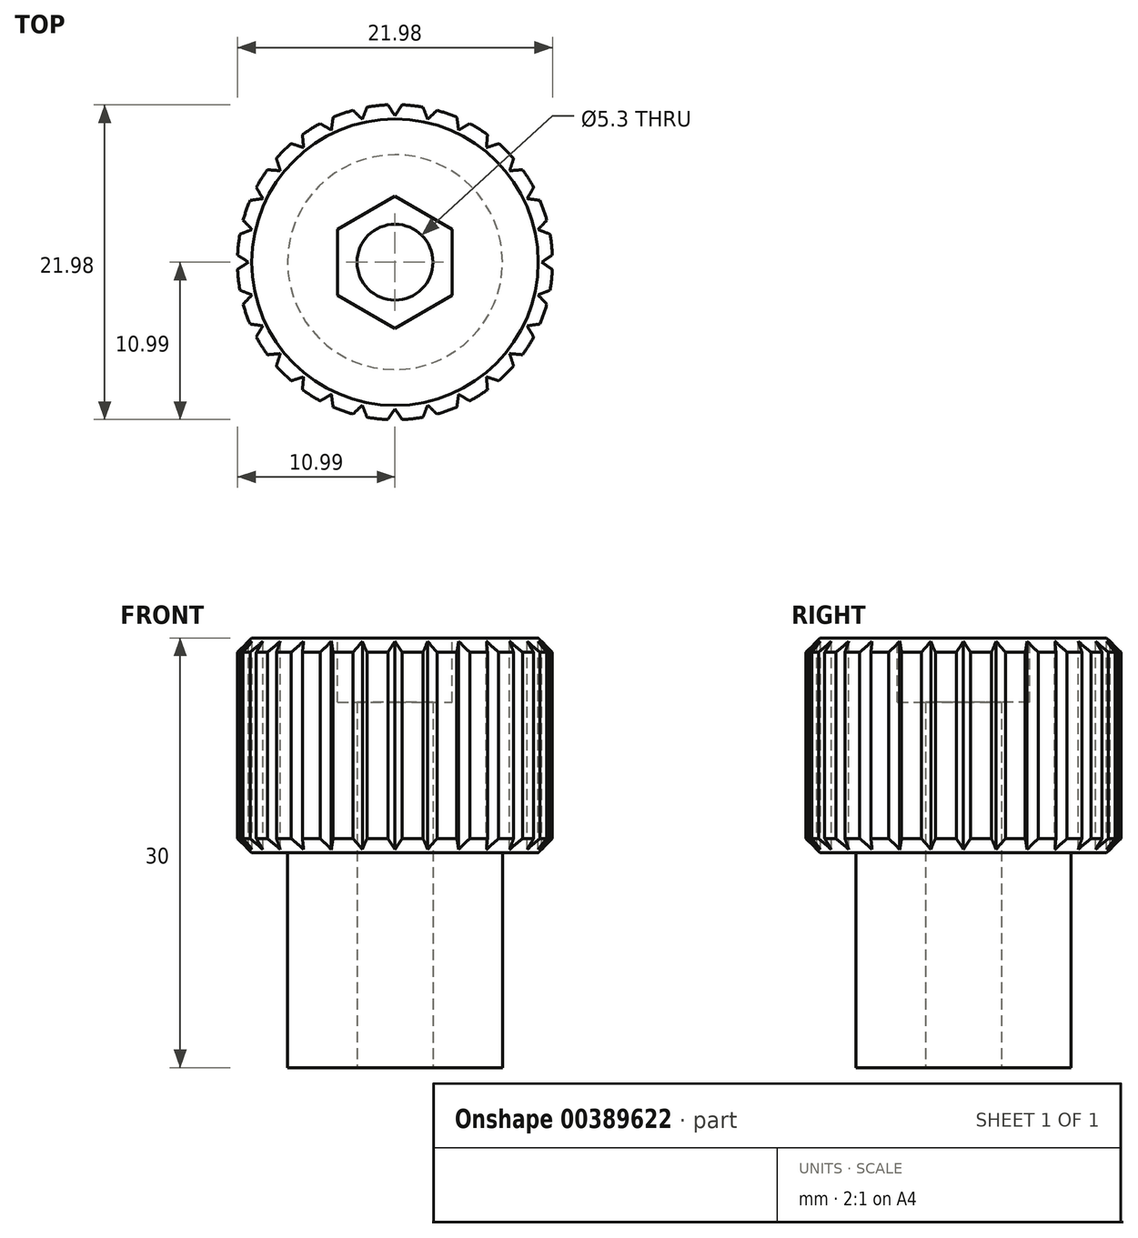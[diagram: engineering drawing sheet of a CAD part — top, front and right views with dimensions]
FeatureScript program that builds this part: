
annotation { "Feature Type Name" : "Feature", "Feature Type Description" : "" }
export const myFeature = defineFeature(function(context is Context, id is Id, definition is map)
    precondition{}
    {
        {
            var Q0;
            Q0=qCreatedBy(makeId("Top.planeOp"),FACE);
            var sketch = newSketch(context, id + "F0", { "sketchPlane" : qUnion([Q0])});
            skCircle(sketch, "E0", {"center": v(0, 0) * mm, "radius": 2.65 * mm});
            skCircle(sketch, "E1", {"center": v(0, 0) * mm, "radius": 7.5 * mm});
            skSolve(sketch);
        }
        {
            var Q0;
            Q0 = qSketchRegion(id + "F0", true);
            extrude(context, id + "F1", {"entities" : qUnion([Q0]), "depth" : 15 * mm});
        }
        {
            var Q0;
            Q0=makeQuery(id+"F1.opExtrude","CAP_FACE",FACE,{"disambiguationData":[OSD([sQuery(id+"F0.wireOp",EDGE,"E0"),sQuery(id+"F0.wireOp",EDGE,"E1")])],"isStart":false});
            var sketch = newSketch(context, id + "F2", { "sketchPlane" : qUnion([Q0])});
            skCircle(sketch, "E2", {"center": v(0, 0) * mm, "radius": 11 * mm});
            skSolve(sketch);
        }
        {
            var Q0;
            Q0 = qSketchRegion(id + "F2", true);
            extrude(context, id + "F3", {"entities" : qUnion([Q0]), "operationType" : NewBodyOperationType.ADD, "depth" : 15 * mm});
        }
        {
            var Q0;
            Q0 = qSketchRegion(id + "F2", true);
            extrude(context, id + "F4", {"entities" : qUnion([Q0]), "operationType" : NewBodyOperationType.ADD, "depth" : 15 * mm});
        }
        {
            var Q0;
            Q0=makeQuery(id+"F3.opExtrude","CAP_FACE",FACE,{"disambiguationData":[OSD([sQuery(id+"F2.wireOp",EDGE,"E2")])],"isStart":false});
            var sketch = newSketch(context, id + "F5", { "sketchPlane" : qUnion([Q0])});
            skCircle(sketch, "E3.cCircle", {"center": v(0, 0) * mm, "radius": 4 * mm, "construction": true});
            skLineSegment(sketch, "E3.0", {"start": v(4, 2.3) * mm, "end": v(4, -2.3) * mm});
            skLineSegment(sketch, "E3.1", {"start": v(4, -2.3) * mm, "end": v(0, -4.62) * mm});
            skLineSegment(sketch, "E3.2", {"start": v(0, -4.62) * mm, "end": v(-4, -2.3) * mm});
            skLineSegment(sketch, "E3.3", {"start": v(-4, -2.3) * mm, "end": v(-4, 2.3) * mm});
            skLineSegment(sketch, "E3.4", {"start": v(-4, 2.3) * mm, "end": v(0, 4.62) * mm});
            skLineSegment(sketch, "E3.5", {"start": v(0, 4.62) * mm, "end": v(4, 2.3) * mm});
            skPoint(sketch, "E3.0.midPoint", {"position": v(4, 0) * mm});
            skSolve(sketch);
        }
        {
            var Q0;
            Q0 = qSketchRegion(id + "F5", true);
            extrude(context, id + "F6", {"entities" : qUnion([Q0]), "operationType" : NewBodyOperationType.REMOVE, "oppositeDirection" : true, "depth" : 4.5 * mm});
        }
        {
            var Q0;
            Q0=makeQuery(id+"F3.opExtrude","CAP_EDGE",EDGE,{"disambiguationData":[OSD([sQuery(id+"F2.wireOp",EDGE,"E2")])],"isStart":false});
            var Q1;
            Q1=makeQuery(id+"F3.opExtrude","CAP_EDGE",EDGE,{"disambiguationData":[OSD([sQuery(id+"F2.wireOp",EDGE,"E2")])],"isStart":true});
            chamfer(context, id + "F7", {"entities" : qUnion([Q0, Q1]), "width" : 1 * mm, "tangentPropagation" : true});
        }
        {
            var Q0;
            Q0=makeQuery(id+"F3.opExtrude","CAP_FACE",FACE,{"disambiguationData":[OSD([sQuery(id+"F2.wireOp",EDGE,"E2")])],"isStart":false});
            var sketch = newSketch(context, id + "F8", { "sketchPlane" : qUnion([Q0])});
            skLineSegment(sketch, "E4", {"start": v(-0.5, -10.99) * mm, "end": v(0, -10.24) * mm});
            skLineSegment(sketch, "E5", {"start": v(0, -10.24) * mm, "end": v(0.5, -10.99) * mm});
            skLineSegment(sketch, "E6", {"start": v(0.5, -10.99) * mm, "end": v(0, -11.74) * mm});
            skLineSegment(sketch, "E7", {"start": v(0, -11.74) * mm, "end": v(-0.5, -10.99) * mm});
            skLineSegment(sketch, "E8", {"start": v(-0.5, -10.99) * mm, "end": v(0.5, -10.99) * mm, "construction": true});
            skLineSegment(sketch, "E9.1.0", {"start": v(2.61, -11.44) * mm, "end": v(1.96, -10.82) * mm});
            skLineSegment(sketch, "E9.1.1", {"start": v(1.96, -10.82) * mm, "end": v(2.28, -9.98) * mm});
            skLineSegment(sketch, "E9.1.2", {"start": v(2.28, -9.98) * mm, "end": v(2.93, -10.6) * mm});
            skLineSegment(sketch, "E9.1.3", {"start": v(2.93, -10.6) * mm, "end": v(2.61, -11.44) * mm});
            skLineSegment(sketch, "E9.1.4", {"start": v(1.96, -10.82) * mm, "end": v(2.93, -10.6) * mm, "construction": true});
            skLineSegment(sketch, "E9.2.0", {"start": v(5.1, -10.58) * mm, "end": v(4.32, -10.12) * mm});
            skLineSegment(sketch, "E9.2.1", {"start": v(4.32, -10.12) * mm, "end": v(4.44, -9.22) * mm});
            skLineSegment(sketch, "E9.2.2", {"start": v(4.44, -9.22) * mm, "end": v(5.22, -9.68) * mm});
            skLineSegment(sketch, "E9.2.3", {"start": v(5.22, -9.68) * mm, "end": v(5.1, -10.58) * mm});
            skLineSegment(sketch, "E9.2.4", {"start": v(4.32, -10.12) * mm, "end": v(5.22, -9.68) * mm, "construction": true});
            skLineSegment(sketch, "E9.3.0", {"start": v(7.32, -9.18) * mm, "end": v(6.46, -8.9) * mm});
            skLineSegment(sketch, "E9.3.1", {"start": v(6.46, -8.9) * mm, "end": v(6.38, -8) * mm});
            skLineSegment(sketch, "E9.3.2", {"start": v(6.38, -8) * mm, "end": v(7.24, -8.28) * mm});
            skLineSegment(sketch, "E9.3.3", {"start": v(7.24, -8.28) * mm, "end": v(7.32, -9.18) * mm});
            skLineSegment(sketch, "E9.3.4", {"start": v(6.46, -8.9) * mm, "end": v(7.24, -8.28) * mm, "construction": true});
            skLineSegment(sketch, "E9.4.0", {"start": v(9.18, -7.32) * mm, "end": v(8.28, -7.24) * mm});
            skLineSegment(sketch, "E9.4.1", {"start": v(8.28, -7.24) * mm, "end": v(8, -6.38) * mm});
            skLineSegment(sketch, "E9.4.2", {"start": v(8, -6.38) * mm, "end": v(8.9, -6.46) * mm});
            skLineSegment(sketch, "E9.4.3", {"start": v(8.9, -6.46) * mm, "end": v(9.18, -7.32) * mm});
            skLineSegment(sketch, "E9.4.4", {"start": v(8.28, -7.24) * mm, "end": v(8.9, -6.46) * mm, "construction": true});
            skLineSegment(sketch, "E9.5.0", {"start": v(10.58, -5.1) * mm, "end": v(9.68, -5.22) * mm});
            skLineSegment(sketch, "E9.5.1", {"start": v(9.68, -5.22) * mm, "end": v(9.22, -4.44) * mm});
            skLineSegment(sketch, "E9.5.2", {"start": v(9.22, -4.44) * mm, "end": v(10.12, -4.32) * mm});
            skLineSegment(sketch, "E9.5.3", {"start": v(10.12, -4.32) * mm, "end": v(10.58, -5.1) * mm});
            skLineSegment(sketch, "E9.5.4", {"start": v(9.68, -5.22) * mm, "end": v(10.12, -4.32) * mm, "construction": true});
            skLineSegment(sketch, "E9.6.0", {"start": v(11.44, -2.61) * mm, "end": v(10.6, -2.93) * mm});
            skLineSegment(sketch, "E9.6.1", {"start": v(10.6, -2.93) * mm, "end": v(9.98, -2.28) * mm});
            skLineSegment(sketch, "E9.6.2", {"start": v(9.98, -2.28) * mm, "end": v(10.82, -1.96) * mm});
            skLineSegment(sketch, "E9.6.3", {"start": v(10.82, -1.96) * mm, "end": v(11.44, -2.61) * mm});
            skLineSegment(sketch, "E9.6.4", {"start": v(10.6, -2.93) * mm, "end": v(10.82, -1.96) * mm, "construction": true});
            skLineSegment(sketch, "E9.7.0", {"start": v(11.74, 0) * mm, "end": v(10.99, -0.5) * mm});
            skLineSegment(sketch, "E9.7.1", {"start": v(10.99, -0.5) * mm, "end": v(10.24, 0) * mm});
            skLineSegment(sketch, "E9.7.2", {"start": v(10.24, 0) * mm, "end": v(10.99, 0.5) * mm});
            skLineSegment(sketch, "E9.7.3", {"start": v(10.99, 0.5) * mm, "end": v(11.74, 0) * mm});
            skLineSegment(sketch, "E9.7.4", {"start": v(10.99, -0.5) * mm, "end": v(10.99, 0.5) * mm, "construction": true});
            skLineSegment(sketch, "E9.8.0", {"start": v(11.44, 2.61) * mm, "end": v(10.82, 1.96) * mm});
            skLineSegment(sketch, "E9.8.1", {"start": v(10.82, 1.96) * mm, "end": v(9.98, 2.28) * mm});
            skLineSegment(sketch, "E9.8.2", {"start": v(9.98, 2.28) * mm, "end": v(10.6, 2.93) * mm});
            skLineSegment(sketch, "E9.8.3", {"start": v(10.6, 2.93) * mm, "end": v(11.44, 2.61) * mm});
            skLineSegment(sketch, "E9.8.4", {"start": v(10.82, 1.96) * mm, "end": v(10.6, 2.93) * mm, "construction": true});
            skLineSegment(sketch, "E9.9.0", {"start": v(10.58, 5.1) * mm, "end": v(10.12, 4.32) * mm});
            skLineSegment(sketch, "E9.9.1", {"start": v(10.12, 4.32) * mm, "end": v(9.22, 4.44) * mm});
            skLineSegment(sketch, "E9.9.2", {"start": v(9.22, 4.44) * mm, "end": v(9.68, 5.22) * mm});
            skLineSegment(sketch, "E9.9.3", {"start": v(9.68, 5.22) * mm, "end": v(10.58, 5.1) * mm});
            skLineSegment(sketch, "E9.9.4", {"start": v(10.12, 4.32) * mm, "end": v(9.68, 5.22) * mm, "construction": true});
            skLineSegment(sketch, "E9.10.0", {"start": v(9.18, 7.32) * mm, "end": v(8.9, 6.46) * mm});
            skLineSegment(sketch, "E9.10.1", {"start": v(8.9, 6.46) * mm, "end": v(8, 6.38) * mm});
            skLineSegment(sketch, "E9.10.2", {"start": v(8, 6.38) * mm, "end": v(8.28, 7.24) * mm});
            skLineSegment(sketch, "E9.10.3", {"start": v(8.28, 7.24) * mm, "end": v(9.18, 7.32) * mm});
            skLineSegment(sketch, "E9.10.4", {"start": v(8.9, 6.46) * mm, "end": v(8.28, 7.24) * mm, "construction": true});
            skLineSegment(sketch, "E9.11.0", {"start": v(7.32, 9.18) * mm, "end": v(7.24, 8.28) * mm});
            skLineSegment(sketch, "E9.11.1", {"start": v(7.24, 8.28) * mm, "end": v(6.38, 8) * mm});
            skLineSegment(sketch, "E9.11.2", {"start": v(6.38, 8) * mm, "end": v(6.46, 8.9) * mm});
            skLineSegment(sketch, "E9.11.3", {"start": v(6.46, 8.9) * mm, "end": v(7.32, 9.18) * mm});
            skLineSegment(sketch, "E9.11.4", {"start": v(7.24, 8.28) * mm, "end": v(6.46, 8.9) * mm, "construction": true});
            skLineSegment(sketch, "E9.12.0", {"start": v(5.1, 10.58) * mm, "end": v(5.22, 9.68) * mm});
            skLineSegment(sketch, "E9.12.1", {"start": v(5.22, 9.68) * mm, "end": v(4.44, 9.22) * mm});
            skLineSegment(sketch, "E9.12.2", {"start": v(4.44, 9.22) * mm, "end": v(4.32, 10.12) * mm});
            skLineSegment(sketch, "E9.12.3", {"start": v(4.32, 10.12) * mm, "end": v(5.1, 10.58) * mm});
            skLineSegment(sketch, "E9.12.4", {"start": v(5.22, 9.68) * mm, "end": v(4.32, 10.12) * mm, "construction": true});
            skLineSegment(sketch, "E9.13.0", {"start": v(2.61, 11.44) * mm, "end": v(2.93, 10.6) * mm});
            skLineSegment(sketch, "E9.13.1", {"start": v(2.93, 10.6) * mm, "end": v(2.28, 9.98) * mm});
            skLineSegment(sketch, "E9.13.2", {"start": v(2.28, 9.98) * mm, "end": v(1.96, 10.82) * mm});
            skLineSegment(sketch, "E9.13.3", {"start": v(1.96, 10.82) * mm, "end": v(2.61, 11.44) * mm});
            skLineSegment(sketch, "E9.13.4", {"start": v(2.93, 10.6) * mm, "end": v(1.96, 10.82) * mm, "construction": true});
            skLineSegment(sketch, "E9.14.0", {"start": v(0, 11.74) * mm, "end": v(0.5, 10.99) * mm});
            skLineSegment(sketch, "E9.14.1", {"start": v(0.5, 10.99) * mm, "end": v(0, 10.24) * mm});
            skLineSegment(sketch, "E9.14.2", {"start": v(0, 10.24) * mm, "end": v(-0.5, 10.99) * mm});
            skLineSegment(sketch, "E9.14.3", {"start": v(-0.5, 10.99) * mm, "end": v(0, 11.74) * mm});
            skLineSegment(sketch, "E9.14.4", {"start": v(0.5, 10.99) * mm, "end": v(-0.5, 10.99) * mm, "construction": true});
            skLineSegment(sketch, "E9.15.0", {"start": v(-2.61, 11.44) * mm, "end": v(-1.96, 10.82) * mm});
            skLineSegment(sketch, "E9.15.1", {"start": v(-1.96, 10.82) * mm, "end": v(-2.28, 9.98) * mm});
            skLineSegment(sketch, "E9.15.2", {"start": v(-2.28, 9.98) * mm, "end": v(-2.93, 10.6) * mm});
            skLineSegment(sketch, "E9.15.3", {"start": v(-2.93, 10.6) * mm, "end": v(-2.61, 11.44) * mm});
            skLineSegment(sketch, "E9.15.4", {"start": v(-1.96, 10.82) * mm, "end": v(-2.93, 10.6) * mm, "construction": true});
            skLineSegment(sketch, "E9.16.0", {"start": v(-5.1, 10.58) * mm, "end": v(-4.32, 10.12) * mm});
            skLineSegment(sketch, "E9.16.1", {"start": v(-4.32, 10.12) * mm, "end": v(-4.44, 9.22) * mm});
            skLineSegment(sketch, "E9.16.2", {"start": v(-4.44, 9.22) * mm, "end": v(-5.22, 9.68) * mm});
            skLineSegment(sketch, "E9.16.3", {"start": v(-5.22, 9.68) * mm, "end": v(-5.1, 10.58) * mm});
            skLineSegment(sketch, "E9.16.4", {"start": v(-4.32, 10.12) * mm, "end": v(-5.22, 9.68) * mm, "construction": true});
            skLineSegment(sketch, "E9.17.0", {"start": v(-7.32, 9.18) * mm, "end": v(-6.46, 8.9) * mm});
            skLineSegment(sketch, "E9.17.1", {"start": v(-6.46, 8.9) * mm, "end": v(-6.38, 8) * mm});
            skLineSegment(sketch, "E9.17.2", {"start": v(-6.38, 8) * mm, "end": v(-7.24, 8.28) * mm});
            skLineSegment(sketch, "E9.17.3", {"start": v(-7.24, 8.28) * mm, "end": v(-7.32, 9.18) * mm});
            skLineSegment(sketch, "E9.17.4", {"start": v(-6.46, 8.9) * mm, "end": v(-7.24, 8.28) * mm, "construction": true});
            skLineSegment(sketch, "E9.18.0", {"start": v(-9.18, 7.32) * mm, "end": v(-8.28, 7.24) * mm});
            skLineSegment(sketch, "E9.18.1", {"start": v(-8.28, 7.24) * mm, "end": v(-8, 6.38) * mm});
            skLineSegment(sketch, "E9.18.2", {"start": v(-8, 6.38) * mm, "end": v(-8.9, 6.46) * mm});
            skLineSegment(sketch, "E9.18.3", {"start": v(-8.9, 6.46) * mm, "end": v(-9.18, 7.32) * mm});
            skLineSegment(sketch, "E9.18.4", {"start": v(-8.28, 7.24) * mm, "end": v(-8.9, 6.46) * mm, "construction": true});
            skLineSegment(sketch, "E9.19.0", {"start": v(-10.58, 5.1) * mm, "end": v(-9.68, 5.22) * mm});
            skLineSegment(sketch, "E9.19.1", {"start": v(-9.68, 5.22) * mm, "end": v(-9.22, 4.44) * mm});
            skLineSegment(sketch, "E9.19.2", {"start": v(-9.22, 4.44) * mm, "end": v(-10.12, 4.32) * mm});
            skLineSegment(sketch, "E9.19.3", {"start": v(-10.12, 4.32) * mm, "end": v(-10.58, 5.1) * mm});
            skLineSegment(sketch, "E9.19.4", {"start": v(-9.68, 5.22) * mm, "end": v(-10.12, 4.32) * mm, "construction": true});
            skLineSegment(sketch, "E9.20.0", {"start": v(-11.44, 2.61) * mm, "end": v(-10.6, 2.93) * mm});
            skLineSegment(sketch, "E9.20.1", {"start": v(-10.6, 2.93) * mm, "end": v(-9.98, 2.28) * mm});
            skLineSegment(sketch, "E9.20.2", {"start": v(-9.98, 2.28) * mm, "end": v(-10.82, 1.96) * mm});
            skLineSegment(sketch, "E9.20.3", {"start": v(-10.82, 1.96) * mm, "end": v(-11.44, 2.61) * mm});
            skLineSegment(sketch, "E9.20.4", {"start": v(-10.6, 2.93) * mm, "end": v(-10.82, 1.96) * mm, "construction": true});
            skLineSegment(sketch, "E9.21.0", {"start": v(-11.74, 0) * mm, "end": v(-10.99, 0.5) * mm});
            skLineSegment(sketch, "E9.21.1", {"start": v(-10.99, 0.5) * mm, "end": v(-10.24, 0) * mm});
            skLineSegment(sketch, "E9.21.2", {"start": v(-10.24, 0) * mm, "end": v(-10.99, -0.5) * mm});
            skLineSegment(sketch, "E9.21.3", {"start": v(-10.99, -0.5) * mm, "end": v(-11.74, 0) * mm});
            skLineSegment(sketch, "E9.21.4", {"start": v(-10.99, 0.5) * mm, "end": v(-10.99, -0.5) * mm, "construction": true});
            skLineSegment(sketch, "E9.22.0", {"start": v(-11.44, -2.61) * mm, "end": v(-10.82, -1.96) * mm});
            skLineSegment(sketch, "E9.22.1", {"start": v(-10.82, -1.96) * mm, "end": v(-9.98, -2.28) * mm});
            skLineSegment(sketch, "E9.22.2", {"start": v(-9.98, -2.28) * mm, "end": v(-10.6, -2.93) * mm});
            skLineSegment(sketch, "E9.22.3", {"start": v(-10.6, -2.93) * mm, "end": v(-11.44, -2.61) * mm});
            skLineSegment(sketch, "E9.22.4", {"start": v(-10.82, -1.96) * mm, "end": v(-10.6, -2.93) * mm, "construction": true});
            skLineSegment(sketch, "E9.23.0", {"start": v(-10.58, -5.1) * mm, "end": v(-10.12, -4.32) * mm});
            skLineSegment(sketch, "E9.23.1", {"start": v(-10.12, -4.32) * mm, "end": v(-9.22, -4.44) * mm});
            skLineSegment(sketch, "E9.23.2", {"start": v(-9.22, -4.44) * mm, "end": v(-9.68, -5.22) * mm});
            skLineSegment(sketch, "E9.23.3", {"start": v(-9.68, -5.22) * mm, "end": v(-10.58, -5.1) * mm});
            skLineSegment(sketch, "E9.23.4", {"start": v(-10.12, -4.32) * mm, "end": v(-9.68, -5.22) * mm, "construction": true});
            skLineSegment(sketch, "E9.24.0", {"start": v(-9.18, -7.32) * mm, "end": v(-8.9, -6.46) * mm});
            skLineSegment(sketch, "E9.24.1", {"start": v(-8.9, -6.46) * mm, "end": v(-8, -6.38) * mm});
            skLineSegment(sketch, "E9.24.2", {"start": v(-8, -6.38) * mm, "end": v(-8.28, -7.24) * mm});
            skLineSegment(sketch, "E9.24.3", {"start": v(-8.28, -7.24) * mm, "end": v(-9.18, -7.32) * mm});
            skLineSegment(sketch, "E9.24.4", {"start": v(-8.9, -6.46) * mm, "end": v(-8.28, -7.24) * mm, "construction": true});
            skLineSegment(sketch, "E9.25.0", {"start": v(-7.32, -9.18) * mm, "end": v(-7.24, -8.28) * mm});
            skLineSegment(sketch, "E9.25.1", {"start": v(-7.24, -8.28) * mm, "end": v(-6.38, -8) * mm});
            skLineSegment(sketch, "E9.25.2", {"start": v(-6.38, -8) * mm, "end": v(-6.46, -8.9) * mm});
            skLineSegment(sketch, "E9.25.3", {"start": v(-6.46, -8.9) * mm, "end": v(-7.32, -9.18) * mm});
            skLineSegment(sketch, "E9.25.4", {"start": v(-7.24, -8.28) * mm, "end": v(-6.46, -8.9) * mm, "construction": true});
            skLineSegment(sketch, "E9.26.0", {"start": v(-5.1, -10.58) * mm, "end": v(-5.22, -9.68) * mm});
            skLineSegment(sketch, "E9.26.1", {"start": v(-5.22, -9.68) * mm, "end": v(-4.44, -9.22) * mm});
            skLineSegment(sketch, "E9.26.2", {"start": v(-4.44, -9.22) * mm, "end": v(-4.32, -10.12) * mm});
            skLineSegment(sketch, "E9.26.3", {"start": v(-4.32, -10.12) * mm, "end": v(-5.1, -10.58) * mm});
            skLineSegment(sketch, "E9.26.4", {"start": v(-5.22, -9.68) * mm, "end": v(-4.32, -10.12) * mm, "construction": true});
            skLineSegment(sketch, "E9.27.0", {"start": v(-2.61, -11.44) * mm, "end": v(-2.93, -10.6) * mm});
            skLineSegment(sketch, "E9.27.1", {"start": v(-2.93, -10.6) * mm, "end": v(-2.28, -9.98) * mm});
            skLineSegment(sketch, "E9.27.2", {"start": v(-2.28, -9.98) * mm, "end": v(-1.96, -10.82) * mm});
            skLineSegment(sketch, "E9.27.3", {"start": v(-1.96, -10.82) * mm, "end": v(-2.61, -11.44) * mm});
            skLineSegment(sketch, "E9.27.4", {"start": v(-2.93, -10.6) * mm, "end": v(-1.96, -10.82) * mm, "construction": true});
            skPoint(sketch, "E9.center", {"position": v(0, 0) * mm});
            skSolve(sketch);
        }
        {
            var Q0;
            Q0 = qSketchRegion(id + "F8", true);
            extrude(context, id + "F9", {"entities" : qUnion([Q0]), "operationType" : NewBodyOperationType.REMOVE, "oppositeDirection" : true, "depth" : 25 * mm});
        }
        {
            var Q0;
            Q0=makeQuery(id+"F6.boolean.opBoolean","COPY",FACE,{"derivedFrom":makeQuery(id+"F6.opExtrude","CAP_FACE",FACE,{"disambiguationData":[OSD([sQuery(id+"F5.wireOp",EDGE,"E3.0"),sQuery(id+"F5.wireOp",EDGE,"E3.1"),sQuery(id+"F5.wireOp",EDGE,"E3.2"),sQuery(id+"F5.wireOp",EDGE,"E3.3"),sQuery(id+"F5.wireOp",EDGE,"E3.4"),sQuery(id+"F5.wireOp",EDGE,"E3.5")])],"isStart":false})});
            var sketch = newSketch(context, id + "F10", { "sketchPlane" : qUnion([Q0])});
            skCircle(sketch, "E10.0", {"center": v(0, 0) * mm, "radius": 2.65 * mm});
            skSolve(sketch);
        }
        {
            var Q0;
            Q0 = qSketchRegion(id + "F10", true);
            extrude(context, id + "F11", {"entities" : qUnion([Q0]), "operationType" : NewBodyOperationType.REMOVE, "oppositeDirection" : true, "depth" : 25 * mm});
        }
    });
